# Revit family: P1354A_Adjustable_3_Hole_Hinge
name_source: partatom
category: Generic Models
units: mm (PartAtom-declared; Revit-internal decimal feet)

## family parameters
Always vertical = No
Can host rebar = No
Cut with Voids When Loaded = No
OmniClass Number = 23.80.30.17.17
OmniClass Title = Cable Trays and Horizontal Racks
Part Type = Normal
Room Calculation Point = No
Round Connector Dimension = Use Diameter
Shared = No
Work Plane-Based = Yes

## types (3) — shared parameters
Default Elevation = 48 "
Description = P1354A - Adjustable 3-Hole Hinge
Disclaimer = http://www.unistrut.us
Height = 0.25 "
L_half = 4 "
Length = 8 "
Manufacturer = Atkore Unistrut
Model = P1354A
Salsify ID1 = US-P1354A
Type Comments = 80_77_27_15
URL = https://www.atkore.com
Weight = 1.09 lbm
Width = 1.625 "

## per-type parameters (varying)
| type | Material | UPC |
| P1354A EG | Electro Galvanized | "786364007861" |
| P1354A GR | Green | "786364007878" |
| P1354A ZD | Zinc Dichromate | "786364045238" |

note: column(s) folded — value = type name in every type: Part Number

## geometry (parser evidence)
native form markers: Sweep x3
no freeform markers — native parametric forms only
